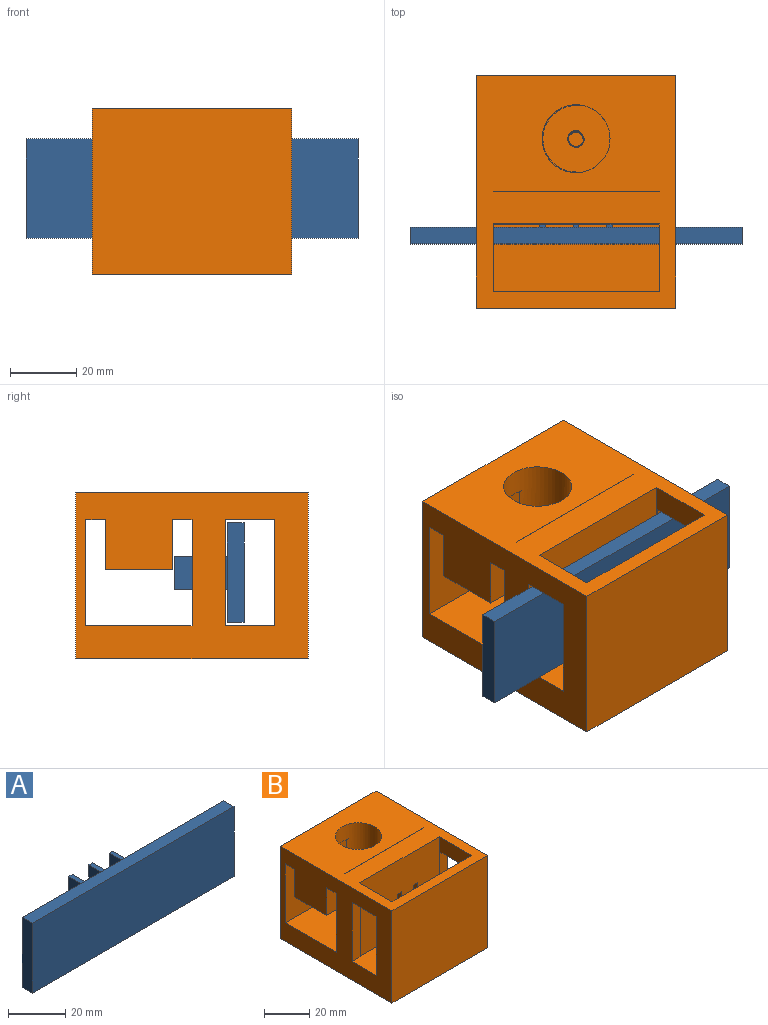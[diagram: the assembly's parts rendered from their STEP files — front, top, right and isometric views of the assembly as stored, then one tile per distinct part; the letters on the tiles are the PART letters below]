
ASSEMBLY  parts=2 mates=1
PART A: 21 faces, bbox 100x21x30 mm
  f0: plane 100x5mm, normal (0,0,1), area 500mm2, adj f1,f3,f4,f5
  f1: plane 30x5mm, normal (-1,0,0), area 150mm2, adj f0,f2,f4,f5
  f2: plane 100x5mm, normal (0,0,-1), area 500mm2, adj f1,f3,f4,f5
  f3: plane 30x5mm, normal (1,0,0), area 150mm2, adj f0,f2,f4,f5
  f4: plane 100x30mm, normal (0,-1,0), area 3000mm2, adj f0,f1,f2,f3
  f5: plane 100x30mm, normal (0,1,0), area 2946mm2, adj f0,f1,f2,f3,f7,f8,f9,f10
  f6: plane 10x1.8mm, normal (0,1,0), area 18mm2, adj f7,f8,f9,f10
  f7: plane 16x1.8mm, normal (0,0,1), area 28.8mm2, adj f5,f6,f8,f10
  f8: plane 16x10mm, normal (-1,0,0), area 160mm2, adj f5,f6,f7,f9
  f9: plane 16x1.8mm, normal (0,0,-1), area 28.8mm2, adj f5,f6,f8,f10
  f10: plane 16x10mm, normal (1,0,0), area 160mm2, adj f5,f6,f7,f9
  f11: plane 10x1.8mm, normal (0,1,0), area 18mm2, adj f12,f13,f14,f15
  f12: plane 16x1.8mm, normal (0,0,1), area 28.8mm2, adj f5,f11,f13,f15
  f13: plane 16x10mm, normal (-1,0,0), area 160mm2, adj f5,f11,f12,f14
  f14: plane 16x1.8mm, normal (0,0,-1), area 28.8mm2, adj f5,f11,f13,f15
  f15: plane 16x10mm, normal (1,0,0), area 160mm2, adj f5,f11,f12,f14
  f16: plane 10x1.8mm, normal (0,1,0), area 18mm2, adj f17,f18,f19,f20
  f17: plane 16x1.8mm, normal (0,0,1), area 28.8mm2, adj f5,f16,f18,f20
  f18: plane 16x10mm, normal (-1,0,0), area 160mm2, adj f5,f16,f17,f19
  f19: plane 16x1.8mm, normal (0,0,-1), area 28.8mm2, adj f5,f16,f18,f20
  f20: plane 16x10mm, normal (1,0,0), area 160mm2, adj f5,f16,f17,f19
PART B: 69 faces, bbox 60.2x70.2x50.2 mm
  f0: plane 60.23x32.23mm, normal (0,0,1), area 1918.8mm2, adj f8,f9,f10,f26,f65,f66,f67,f68
  f1: cylinder r=2.5mm len=5mm, axis (0,0,-1), area 4.3mm2, adj f7,f49,f55
  f2: cylinder r=2.5mm len=5mm, axis (0,0,-1), area 5.5mm2, adj f7,f55,f57
  f3: cylinder r=2.5mm len=5mm, axis (0,0,-1), area 5.5mm2, adj f7,f55,f57
  f4: cylinder r=2.5mm len=5mm, axis (0,0,-1), area 5.5mm2, adj f7,f55,f57
  f5: cylinder r=2.5mm len=5mm, axis (0,0,-1), area 5.5mm2, adj f7,f55,f57
  f6: cylinder r=2.5mm len=5mm, axis (0,0,-1), area 5.5mm2, adj f7,f55,f57
  f7: cylinder r=2.5mm len=5mm, axis (0,0,-1), area 39.6mm2, adj f1,f2,f3,f4,f5,f6,f49,f51
  f8: plane 70x50mm, normal (1,0,0), area 2296mm2, adj f0,f10,f14,f18,f19,f20,f21,f23
  f9: plane 70x50mm, normal (-1,0,0), area 2296mm2, adj f0,f10,f14,f18,f19,f20,f21,f23
  f10: plane 60x40mm, normal (0,1,0), area 2212mm2, adj f0,f8,f9,f15,f16,f20,f23,f36
  f11: plane 50x40mm, normal (0,-1,0), area 1892mm2, adj f12,f13,f14,f20,f36,f37,f38,f39
  f12: plane 40x20.32mm, normal (-1,0,0), area 332.7mm2, adj f11,f14,f17,f20,f33,f34,f35
  f13: plane 40x20.32mm, normal (1,0,0), area 332.7mm2, adj f11,f14,f17,f20,f30,f31,f32
  f14: plane 60x20.32mm, normal (0,0,1), area 1165.9mm2, adj f8,f9,f11,f12,f13,f17,f30,f32
  f15: plane 8x0.05mm, normal (-1,0,0), area 0.4mm2, adj f10,f20,f22,f23
  f16: plane 8x0.05mm, normal (1,0,0), area 0.4mm2, adj f10,f20,f22,f23
  f17: plane 50x40mm, normal (0,1,0), area 2000mm2, adj f12,f13,f14,f20
  f18: plane 60x50mm, normal (0,-1,0), area 3000mm2, adj f8,f9,f20,f21
  f19: plane 60x50mm, normal (0,1,0), area 3000mm2, adj f8,f9,f20,f21
  f20: plane 70x60mm, normal (0,0,1), area 2851.7mm2, adj f8,f9,f10,f11,f12,f13,f15,f16
  f21: plane 70x60mm, normal (0,0,-1), area 4200mm2, adj f8,f9,f18,f19
  f22: plane 50x8mm, normal (0,-1,0), area 400mm2, adj f15,f16,f20,f23
  f23: plane 60x6mm, normal (0,0,-1), area 357mm2, adj f8,f9,f10,f15,f16,f22,f24,f25
  f24: plane 27.75x15mm, normal (0,-1,0), area 416.2mm2, adj f9,f23,f48,f52
  f25: plane 30x15mm, normal (0,-1,0), area 427.5mm2, adj f8,f23,f48,f49,f50,f51
  f26: plane 60x32mm, normal (0,-1,0), area 1920mm2, adj f0,f8,f9,f29
  f27: plane 27.75x15mm, normal (0,1,0), area 416.2mm2, adj f9,f29,f48,f52
  f28: plane 30x15mm, normal (0,1,0), area 427.5mm2, adj f8,f29,f48,f49,f50,f51
  f29: plane 60x6mm, normal (0,0,-1), area 359.2mm2, adj f8,f9,f26,f27,f28,f48
  f30: plane 32x5mm, normal (0,1,0), area 160mm2, adj f9,f13,f14,f31
  f31: plane 15x5mm, normal (0,0,-1), area 75mm2, adj f9,f13,f30,f32
  f32: plane 32x5mm, normal (0,-1,0), area 160mm2, adj f9,f13,f14,f31
  f33: plane 32x5mm, normal (0,-1,0), area 160mm2, adj f8,f12,f14,f34
  f34: plane 15x5mm, normal (0,0,-1), area 75mm2, adj f8,f12,f33,f35
  f35: plane 32x5mm, normal (0,1,0), area 160mm2, adj f8,f12,f14,f34
  f36: plane 9.68x3mm, normal (0,0,1), area 29mm2, adj f10,f11,f37,f39
  f37: plane 12x9.68mm, normal (-1,0,0), area 116.2mm2, adj f10,f11,f36,f38
  f38: plane 9.68x3mm, normal (0,0,-1), area 29mm2, adj f10,f11,f37,f39
  f39: plane 12x9.68mm, normal (1,0,0), area 116.2mm2, adj f10,f11,f36,f38
  f40: plane 9.68x3mm, normal (0,0,1), area 29mm2, adj f10,f11,f41,f43
  f41: plane 12x9.68mm, normal (-1,0,0), area 116.2mm2, adj f10,f11,f40,f42
  f42: plane 9.68x3mm, normal (0,0,-1), area 29mm2, adj f10,f11,f41,f43
  f43: plane 12x9.68mm, normal (1,0,0), area 116.2mm2, adj f10,f11,f40,f42
  f44: plane 9.68x3mm, normal (0,0,1), area 29mm2, adj f10,f11,f45,f47
  f45: plane 12x9.68mm, normal (-1,0,0), area 116.2mm2, adj f10,f11,f44,f46
  f46: plane 9.68x3mm, normal (0,0,-1), area 29mm2, adj f10,f11,f45,f47
  f47: plane 12x9.68mm, normal (1,0,0), area 116.2mm2, adj f10,f11,f44,f46
  f48: cylinder r=10.25mm len=23mm, axis (0,0,-1), area 1206.8mm2, adj f20,f23,f24,f25,f27,f28,f29,f49
  f49: plane 20.34x20.09mm, normal (0,0,1), area 304.2mm2, adj f1,f7,f25,f28,f48,f50,f53,f55
  f50: cylinder r=10mm len=20mm, axis (0,0,-1), area 157.1mm2, adj f25,f28,f49,f51
  f51: plane 40.03x20.03mm, normal (0,0,-1), area 739.5mm2, adj f7,f8,f25,f28,f50,f53,f54,f55
  f52: plane 27.75x20mm, normal (0,0,-1), area 435.7mm2, adj f9,f24,f27,f48
  f53: cylinder r=2.29mm len=5mm, axis (0,0,-1), area 42mm2, adj f49,f51,f55,f56,f57
  f54: cylinder r=2.5mm len=5mm, axis (0,0,-1), area 2.7mm2, adj f7,f51,f57
  f55: bspline ~5.77x5.45mm, area 23.3mm2, adj f1,f2,f3,f4,f5,f6,f49,f51
  f56: plane 0.22x0.17mm, normal (0,1,-0.05), area 0mm2, adj f49,f53,f57,f64
  f57: bspline ~5.77x5.32mm, area 22.9mm2, adj f2,f3,f4,f5,f6,f51,f53,f54
  f58: bspline ~5.05x3.75mm, area 0.4mm2, adj f7,f51,f55,f57
  f59: bspline ~5.05x5mm, area 0.8mm2, adj f7,f55,f57
  f60: bspline ~5.05x5mm, area 0.8mm2, adj f7,f55,f57
  f61: bspline ~5.05x5mm, area 0.8mm2, adj f7,f55,f57
  f62: bspline ~5.05x5mm, area 0.8mm2, adj f7,f55,f57
  f63: bspline ~5.05x5mm, area 0.8mm2, adj f7,f55,f57
  f64: bspline ~7.09x5.01mm, area 0.8mm2, adj f7,f49,f55,f56,f57
  f65: plane 0.43x0.3mm, normal (0,1,0.05), area 0.1mm2, adj f0,f66,f67,f68
  f66: bspline ~4.15x2.4mm, area 0.7mm2, adj f0,f65,f67
  f67: bspline ~5.05x5mm, area 1.5mm2, adj f0,f65,f66,f68
  f68: bspline ~2.17x1.25mm, area 0mm2, adj f0,f65,f67
PLACE A t=(-0.01,0.32,0)mm
PLACE B at identity fixed
MATE slider A.f5 <-> B.f32  axis (0,-1,0) through (-0.01,-10.68,26)mm
